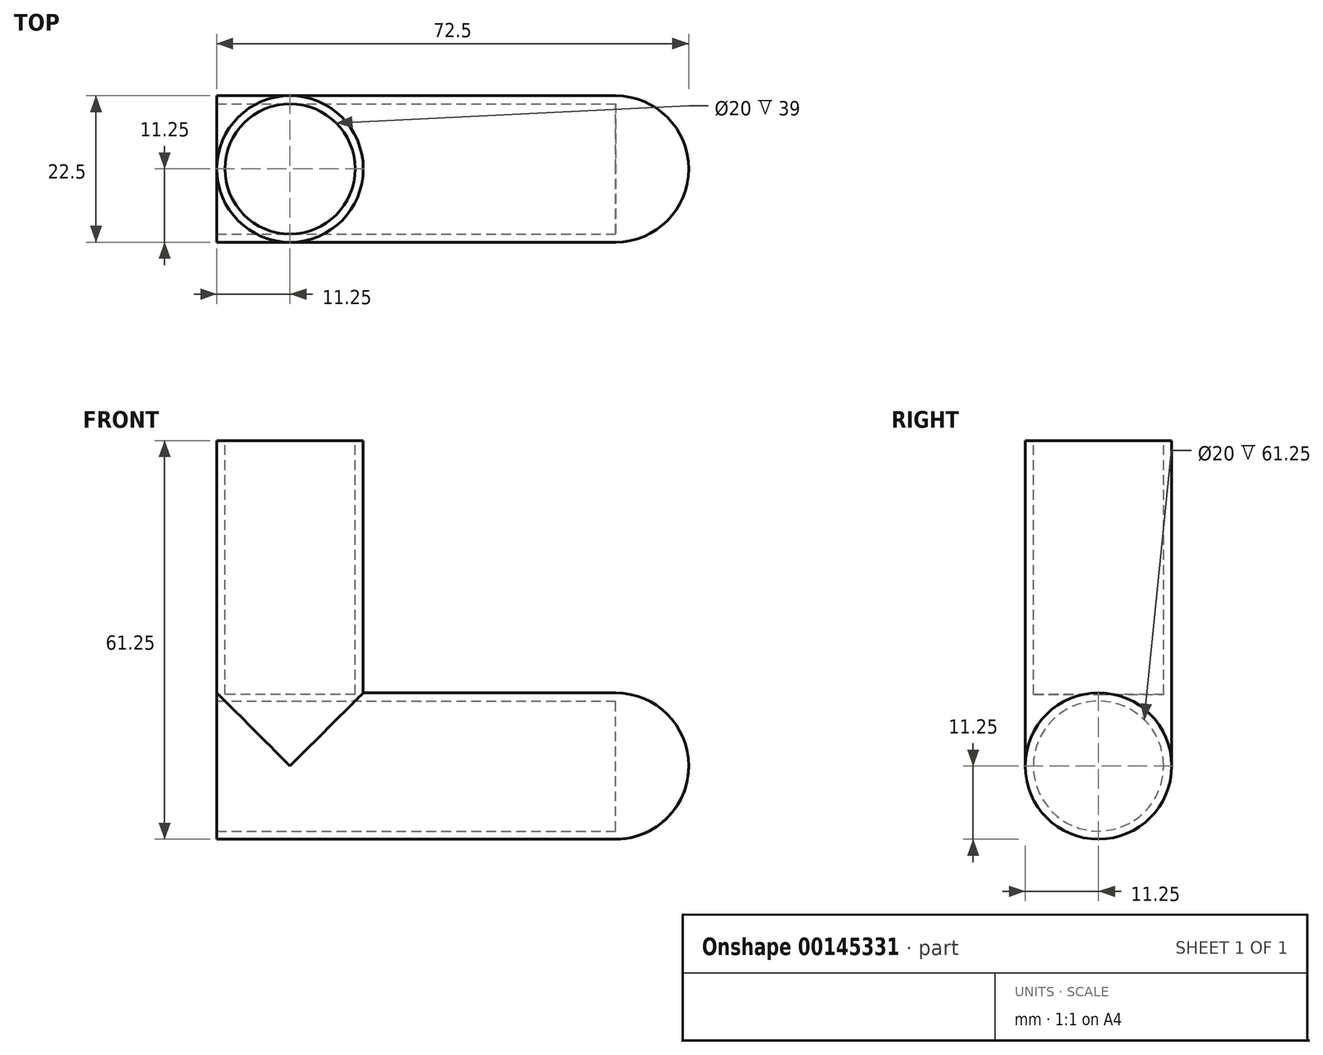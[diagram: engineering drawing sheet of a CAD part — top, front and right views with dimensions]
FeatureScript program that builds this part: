
annotation { "Feature Type Name" : "Feature", "Feature Type Description" : "" }
export const myFeature = defineFeature(function(context is Context, id is Id, definition is map)
    precondition{}
    {
        {
            var Q0;
            Q0=qCreatedBy(makeId("Right.planeOp"),FACE);
            var sketch = newSketch(context, id + "F0", { "sketchPlane" : qUnion([Q0])});
            skCircle(sketch, "E0", {"center": v(0, 0) * mm, "radius": 11.25 * mm});
            skSolve(sketch);
        }
        {
            var Q0;
            Q0 = qSketchRegion(id + "F0", true);
            extrude(context, id + "F1", {"entities" : qUnion([Q0]), "depth" : 50 * mm, "hasSecondDirection" : true, "secondDirectionOppositeDirection" : true, "secondDirectionDepth" : 11.25 * mm});
        }
        {
            var Q0;
            Q0=qCreatedBy(makeId("Top.planeOp"),FACE);
            var sketch = newSketch(context, id + "F2", { "sketchPlane" : qUnion([Q0])});
            skCircle(sketch, "E1", {"center": v(0, 0) * mm, "radius": 11.25 * mm});
            skSolve(sketch);
        }
        {
            var Q0;
            Q0 = qSketchRegion(id + "F2", true);
            extrude(context, id + "F3", {"entities" : qUnion([Q0]), "operationType" : NewBodyOperationType.ADD, "depth" : 50 * mm});
        }
        {
            var Q0;
            Q0=makeQuery(id+"F3.opExtrude","CAP_FACE",FACE,{"disambiguationData":[OSD([sQuery(id+"F2.wireOp",EDGE,"E1")])],"isStart":false});
            cPlane(context, id + "F4", {"entities" : qUnion([Q0]), "cplaneType" : CPlaneType.OFFSET, "offset" : 0 * mm, "width" : 150 * mm, "height" : 150 * mm});
        }
        {
            var Q0;
            Q0=qCreatedBy(id+"F4.planeOp",FACE);
            var sketch = newSketch(context, id + "F5", { "sketchPlane" : qUnion([Q0])});
            skCircle(sketch, "E2", {"center": v(0, 0) * mm, "radius": 10 * mm});
            skSolve(sketch);
        }
        {
            var Q0;
            Q0 = qSketchRegion(id + "F5", true);
            extrude(context, id + "F6", {"entities" : qUnion([Q0]), "operationType" : NewBodyOperationType.REMOVE, "oppositeDirection" : true, "depth" : 39 * mm});
        }
        {
            var Q0;
            Q0=makeQuery(id+"F1.opExtrude","CAP_FACE",FACE,{"disambiguationData":[OSD([sQuery(id+"F0.wireOp",EDGE,"E0")])],"isStart":false});
            cPlane(context, id + "F7", {"entities" : qUnion([Q0]), "cplaneType" : CPlaneType.OFFSET, "offset" : 0 * mm, "width" : 150 * mm, "height" : 150 * mm});
        }
        {
            var Q0;
            Q0=qCreatedBy(id+"F7.planeOp",FACE);
            var sketch = newSketch(context, id + "F8", { "sketchPlane" : qUnion([Q0])});
            skCircle(sketch, "E3", {"center": v(0, 0) * mm, "radius": 10 * mm});
            skSolve(sketch);
        }
        {
            var Q0;
            Q0=makeQuery(id+"F8.imprint","IMPRINT",FACE,{"disambiguationData":[TD([[makeQuery(id+"F8.imprint","IMPRINT",EDGE,{"derivedFrom":sQuery(id+"F8.wireOp",EDGE,"E3")}),1.0]])]});
            extrude(context, id + "F9", {"entities" : qUnion([Q0]), "operationType" : NewBodyOperationType.REMOVE, "oppositeDirection" : true, "depth" : 62.75 * mm});
        }
        {
            var Q0;
            Q0=qCreatedBy(makeId("Front.planeOp"),FACE);
            var sketch = newSketch(context, id + "F10", { "sketchPlane" : qUnion([Q0])});
            skLineSegment(sketch, "E4.0", {"start": v(50, 11.25) * mm, "end": v(50, 0) * mm});
            skArc(sketch, "E5", {"start": v(61.25, 0) * mm, "mid": v(57.95, 7.95) * mm, "end": v(50, 11.25) * mm});
            skLineSegment(sketch, "E6", {"start": v(50, 0) * mm, "end": v(61.25, 0) * mm});
            skLineSegment(sketch, "E7", {"start": v(50, 0) * mm, "end": v(67.47, 0) * mm, "construction": true});
            skSolve(sketch);
        }
        {
            var Q0;
            Q0=makeQuery(id+"F10.imprint","IMPRINT",FACE,{"disambiguationData":[TD([[makeQuery(id+"F10.imprint","IMPRINT",EDGE,{"derivedFrom":sQuery(id+"F10.wireOp",EDGE,"E4.0")}),1.0]])]});
            var Q1;
            Q1=sQuery(id+"F10.wireOp",EDGE,"E7");
            revolve(context, id + "F11", {"operationType" : NewBodyOperationType.ADD, "entities" : qUnion([Q0]), "axis" : qUnion([Q1]), "revolveType" : RevolveType.FULL});
        }
    });
